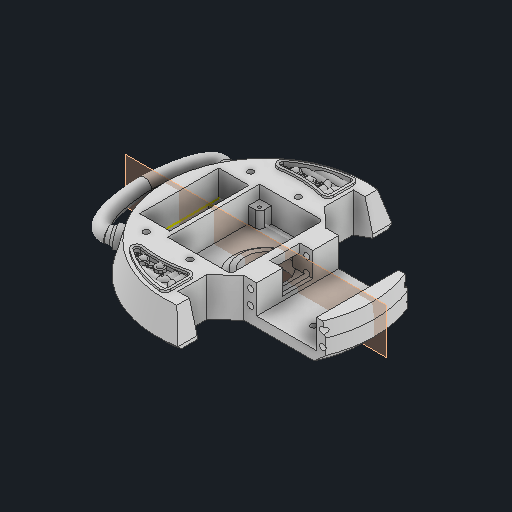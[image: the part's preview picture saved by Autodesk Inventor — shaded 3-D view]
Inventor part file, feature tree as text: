
AUTODESK INVENTOR PART (.ipt)
format: ipt  version: 2024 (Build 280153000, 153)  size: 1,223,680 bytes
history: native  units: in
note: dims shown in document units (in); Inventor stores cm internally (conversion verified against a paired STEP export)
features: sketch x30, projected_geometry x28, extrude x25, sweep x5, mirror x3, chamfer x3, fillet x3, plane x3, other x3, revolve x2, reference x2
ambient origin geometry x8: Origin, YZ Plane, XZ Plane, XY Plane, X Axis, Y Axis, Z Axis, Center Point
bodies: Solid1 (feature_tree)
feature tree (107):
  extrude  "Extrusion1"  Depth=1.6063in
  sketch  "Sketch3"  dims[d2=1.55in d3=1.1319in]
  extrude  "Extrusion2"  Depth=1.1319in
  extrude  "Extrusion3"  Depth=0.2559in
  extrude  "Extrusion4"  Depth=0.0079in
  mirror  "Mirror1"
  extrude  "Extrusion5"  Depth=0.0079in
  sketch  "Sketch6"  dims[d8=0.0157in d9=0.0079in]
  sketch  "Sketch7"  dims[d10=0.7874in d11=0.0in d12=0.2756in d13=-0.3092in]
  extrude  "Extrusion6"  Depth=0.2756in
  extrude  "Extrusion7"  Depth=0.7874in TaperAngle=0.0deg
  extrude  "Extrusion8"  Depth=0.4134in
  sketch  "Sketch10"  dims[d14=0.7874in d15=-0.1031in d16=0.7874in d17=0.0in]
  extrude  "Extrusion9"  Depth=0.7874in TaperAngle=0.0deg
  extrude  "Extrusion10"  Depth=0.3937in TaperAngle=0.0deg
  extrude  "Extrusion11"  Depth=1.5748in
  extrude  "Extrusion12"  Depth=0.2756in
  extrude  "Extrusion13"  Depth=0.7874in
  extrude  "Extrusion14"  Depth=0.7874in
  extrude  "Extrusion15"  Depth=1.0in TaperAngle=0.0deg
  sketch  "Sketch18"  dims[d43=0.2756in d44=0.7874in]
  extrude  "Extrusion16"  Depth=0.1673in
  extrude  "Extrusion17"  Depth=0.1673in
  extrude  "Extrusion18"  Depth=1.128in
  chamfer  "Chamfer1"  Distance=0.7874in
  extrude  "Extrusion19"  Depth=0.1161in
  fillet  "Fillet2"  Radius=0.1161in
  extrude  "Extrusion20"  Depth=0.0787in TaperAngle=0.0deg
  fillet  "Fillet3"  Radius=0.0394in
  extrude  "Extrusion21"  Depth=1.1447in
  chamfer  "Chamfer2"  Distance=0.3912in
  plane  "Work Plane1"
  sketch  "Sketch24"  dims[d55=0.5906in d56=0.0in d57=1.128in]
  sketch  "Sketch25"  dims[d58=2.0394in]
  sketch  "Sketch26"  dims[d59=1.5748in]
  extrude  "Extrusion22"  Depth=0.0492in TaperAngle=0.0deg
  sweep  "Sweep1"
  sweep  "Sweep2"
  plane  "Work Plane2"
  sweep  "Sweep3"
  sketch  "Sketch28"  dims[d61=0.0787in d62=0.7874in d63=0.0in]
  extrude  "Extrusion23"  Depth=0.0787in
  extrude  "Extrusion24"  Depth=0.0787in
  fillet  "Fillet4"  Radius=0.3979in
  sketch  "Sketch29"  dims[d64=0.0886in d65=0.1161in d66=0.1161in]
  revolve  "Revolution1"  [1 undecoded]
  revolve  "Revolution2"  [1 undecoded]
  extrude  "Extrusion25"  Depth=0.0787in
  mirror  "Mirror2"
  sketch  "Sketch31"  dims[d72=0.345in d73=0.0in d74=1.1447in d75=0.3912in d76=0.0in]
  plane  "Work Plane3"
  sweep  "Sweep4"
  sketch  "Sketch34"  dims[d83=0.1654in d84=0.4724in d85=0.0in]
  sketch  "Sketch35"  dims[d86=0.375in d87=0.0625in d88=45.0deg d89=0.1378in]
  sweep  "Sweep5"
  chamfer  "Chamfer3"  Distance=0.1969in
  mirror  "Mirror3"
  sketch  "Sketch36"  dims[d90=0.4331in d91=0.0in d92=0.1875in d94=0.1673in d95=0.3979in d96=0.1673in d97=0.1673in d98=0.1673in d99=0.3979in d100=0.1772in d101=0.1969in d102=0.0in d103=0.0787in d104=0.1772in d105=0.1654in d106=0.1654in d107=0.315in d108=0.0in d109=0.1654in d110=0.5in d111=0.125in d112=0.1374in d113=0.125in d114=0.1575in d115=0.125in d116=0.1575in d117=0.1969in d118=0.0965in d119=0.0in d120=0.0in d121=0.0in d122=0.0in d123=0.0in d124=-0.5118in d125=0.1575in d126=0.0in d127=0.0in d128=0.0394in d129=0.0in d130=0.0866in d131=0.0in d132=0.0197in d133=90.0deg d134=90.0deg d135=0.0689in d136=0.0591in d137=0.0in d138=0.0412in d139=0.3839in d140=0.0in d141=0.0in d142=0.0787in d143=0.0787in d144=0.0in d145=0.0in d146=0.0394in d147=0.125in d148=0.0344in]
  sketch  "Sketch2"  dims[d0=5.5118in d1=1.6063in]
  projected_geometry  "Projected Loop1"
  projected_geometry  "Projected Loop2"
  sketch  "Sketch4"  dims[d4=0.126in d5=0.2559in]
  sketch  "Sketch5"  dims[d6=0.2559in d7=0.0079in]
  projected_geometry  "Projected Loop3"
  projected_geometry  "Projected Loop4"
  projected_geometry  "Projected Loop5"
  projected_geometry  "Projected Loop6"
  projected_geometry  "Projected Loop7"
  projected_geometry  "Projected Loop8"
  projected_geometry  "Projected Loop11"
  sketch  "Sketch11"  dims[d18=0.7874in d19=0.0in d20=0.4134in]
  projected_geometry  "Projected Loop12"
  sketch  "Sketch12"  dims[d21=0.1181in d26=0.7874in d27=0.0in]
  sketch  "Sketch13"  dims[d30=1.0in d31=0.0in d37=0.3937in d38=0.0in]
  projected_geometry  "Projected Loop13"
  sketch  "Sketch14"  dims[d39=0.7874in d40=1.5748in]
  projected_geometry  "Projected Loop14"
  projected_geometry  "Projected Loop15"
  projected_geometry  "Projected Loop16"
  sketch  "Sketch15"  dims[d41=0.0197in d42=0.2756in]
  projected_geometry  "Projected Loop17"
  sketch  "Sketch19"  dims[d45=0.0197in d46=0.7874in]
  projected_geometry  "Projected Loop19"
  sketch  "Sketch21"  dims[d47=0.0197in d48=1.0in d49=0.0in]
  projected_geometry  "Projected Loop23"
  sketch  "Sketch22"  dims[d50=0.7087in d51=0.0in d52=0.1673in]
  reference  "Reference1"
  projected_geometry  "Projected Loop24"
  reference  "Reference2"
  sketch  "Sketch23"  dims[d53=0.1673in d54=0.1673in]
  projected_geometry  "Projected Loop25"
  projected_geometry  "Projected Loop26"
  projected_geometry  "Projected Loop27"
  projected_geometry  "Projected Loop28"
  sketch  "Sketch27"  dims[d60=2.3622in]
  projected_geometry  "Projected Loop29"
  projected_geometry  "Projected Loop30"
  projected_geometry  "Projected Loop31"
  sketch  "Sketch30"  dims[d67=0.0787in d68=0.4331in d69=0.0in d70=0.0394in d71=0.0in]
  projected_geometry  "Projected Loop32"
  sketch  "Sketch32"  dims[d77=0.0492in d78=0.0492in d79=0.0in]
  projected_geometry  "Projected Loop33"
  sketch  "Sketch33"  dims[d80=0.1654in d82=0.1654in]
  projected_geometry  "Projected Loop34"
  other  "<userpath>\Desktop\Camera_Mount.iam"
  other  "Camera_Mount.iam"
  other  "Neck_Cover:1"
note: 2 required parameter values undecoded (feature->parameter linkage not recoverable at this tier; creation-order binding heuristic only, values carry confidence <= 0.55)
